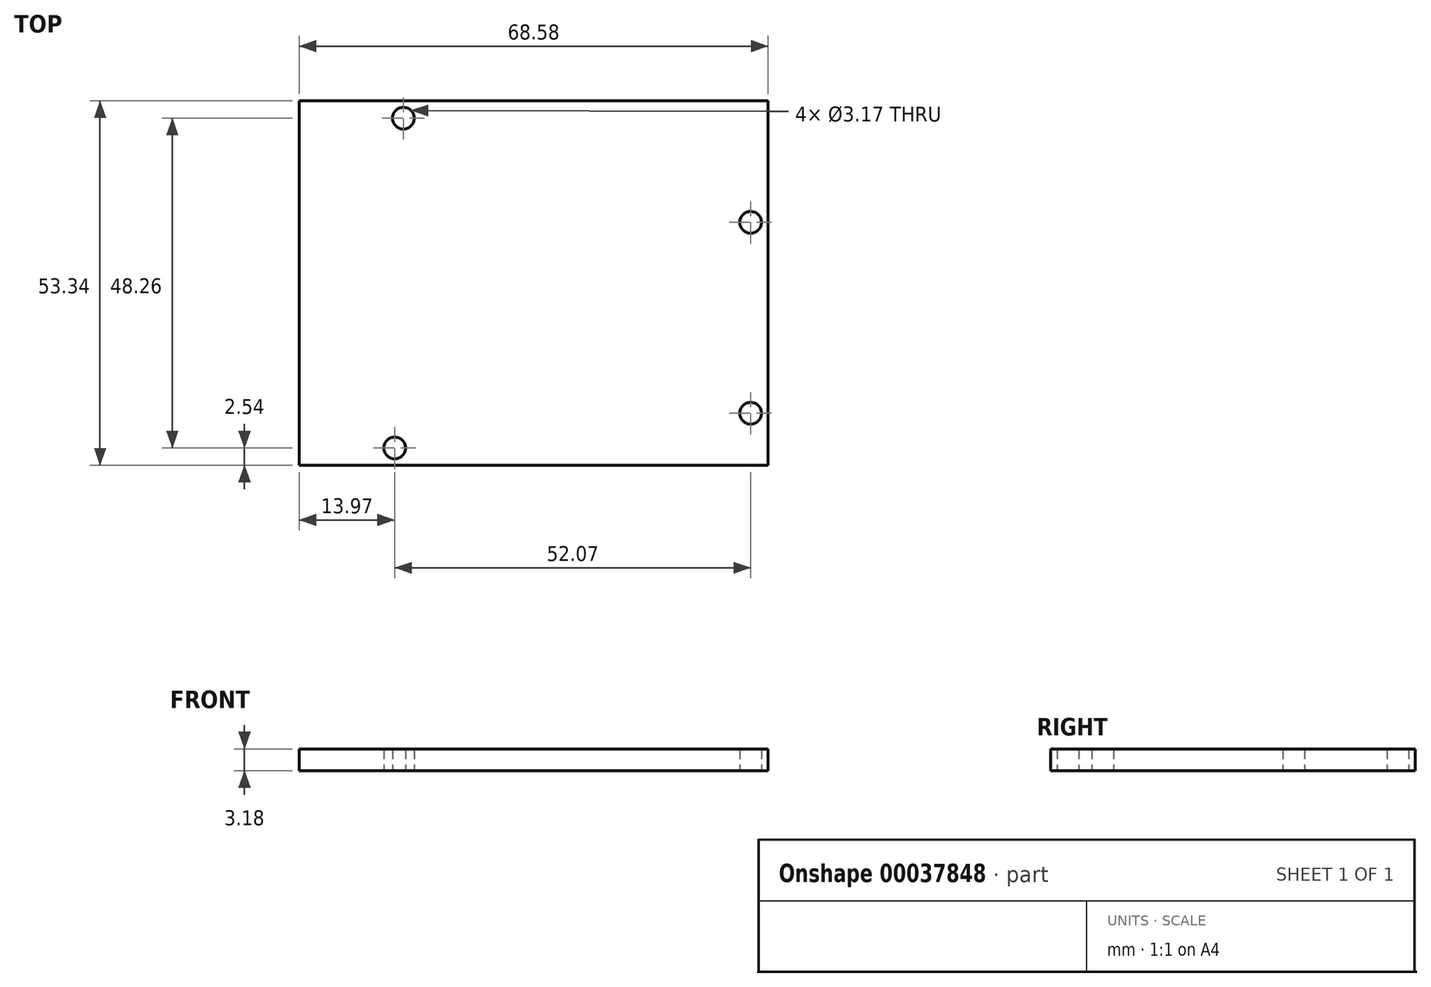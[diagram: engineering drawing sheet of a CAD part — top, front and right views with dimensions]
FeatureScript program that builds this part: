
annotation { "Feature Type Name" : "Feature", "Feature Type Description" : "" }
export const myFeature = defineFeature(function(context is Context, id is Id, definition is map)
    precondition{}
    {
        {
            var Q0;
            Q0=qCreatedBy(makeId("Top.planeOp"),FACE);
            var sketch = newSketch(context, id + "F0", { "sketchPlane" : qUnion([Q0])});
            skLineSegment(sketch, "E0.bottom", {"start": v(0, 0) * mm, "end": v(68.58, 0) * mm});
            skLineSegment(sketch, "E0.top", {"start": v(0, -53.34) * mm, "end": v(68.58, -53.34) * mm});
            skLineSegment(sketch, "E0.left", {"start": v(0, 0) * mm, "end": v(0, -53.34) * mm});
            skLineSegment(sketch, "E0.right", {"start": v(68.58, 0) * mm, "end": v(68.58, -53.34) * mm});
            skLineSegment(sketch, "E1", {"start": v(66.04, -45.72) * mm, "end": v(66.04, -17.78) * mm});
            skCircle(sketch, "E2", {"center": v(66.04, -45.72) * mm, "radius": 1.59 * mm});
            skCircle(sketch, "E3", {"center": v(66.04, -17.78) * mm, "radius": 1.59 * mm});
            skCircle(sketch, "E4", {"center": v(15.24, -2.54) * mm, "radius": 1.59 * mm});
            skCircle(sketch, "E5", {"center": v(13.97, -50.8) * mm, "radius": 1.59 * mm});
            skLineSegment(sketch, "E6", {"start": v(13.97, -53.34) * mm, "end": v(13.97, -50.8) * mm, "construction": true});
            skLineSegment(sketch, "E7", {"start": v(13.97, -50.8) * mm, "end": v(13.97, -2.54) * mm, "construction": true});
            skLineSegment(sketch, "E8", {"start": v(13.97, -2.54) * mm, "end": v(15.24, -2.54) * mm, "construction": true});
            skLineSegment(sketch, "E9", {"start": v(15.24, -2.54) * mm, "end": v(66.04, -2.54) * mm, "construction": true});
            skLineSegment(sketch, "E10", {"start": v(66.04, -2.54) * mm, "end": v(66.04, -17.78) * mm, "construction": true});
            skLineSegment(sketch, "E11", {"start": v(66.04, -45.72) * mm, "end": v(66.04, -53.34) * mm, "construction": true});
            skSolve(sketch);
        }
        {
            var Q0;
            Q0 = qSketchRegion(id + "F0", true);
            extrude(context, id + "F1", {"entities" : qUnion([Q0]), "depth" : 3.17 * mm});
        }
    });
